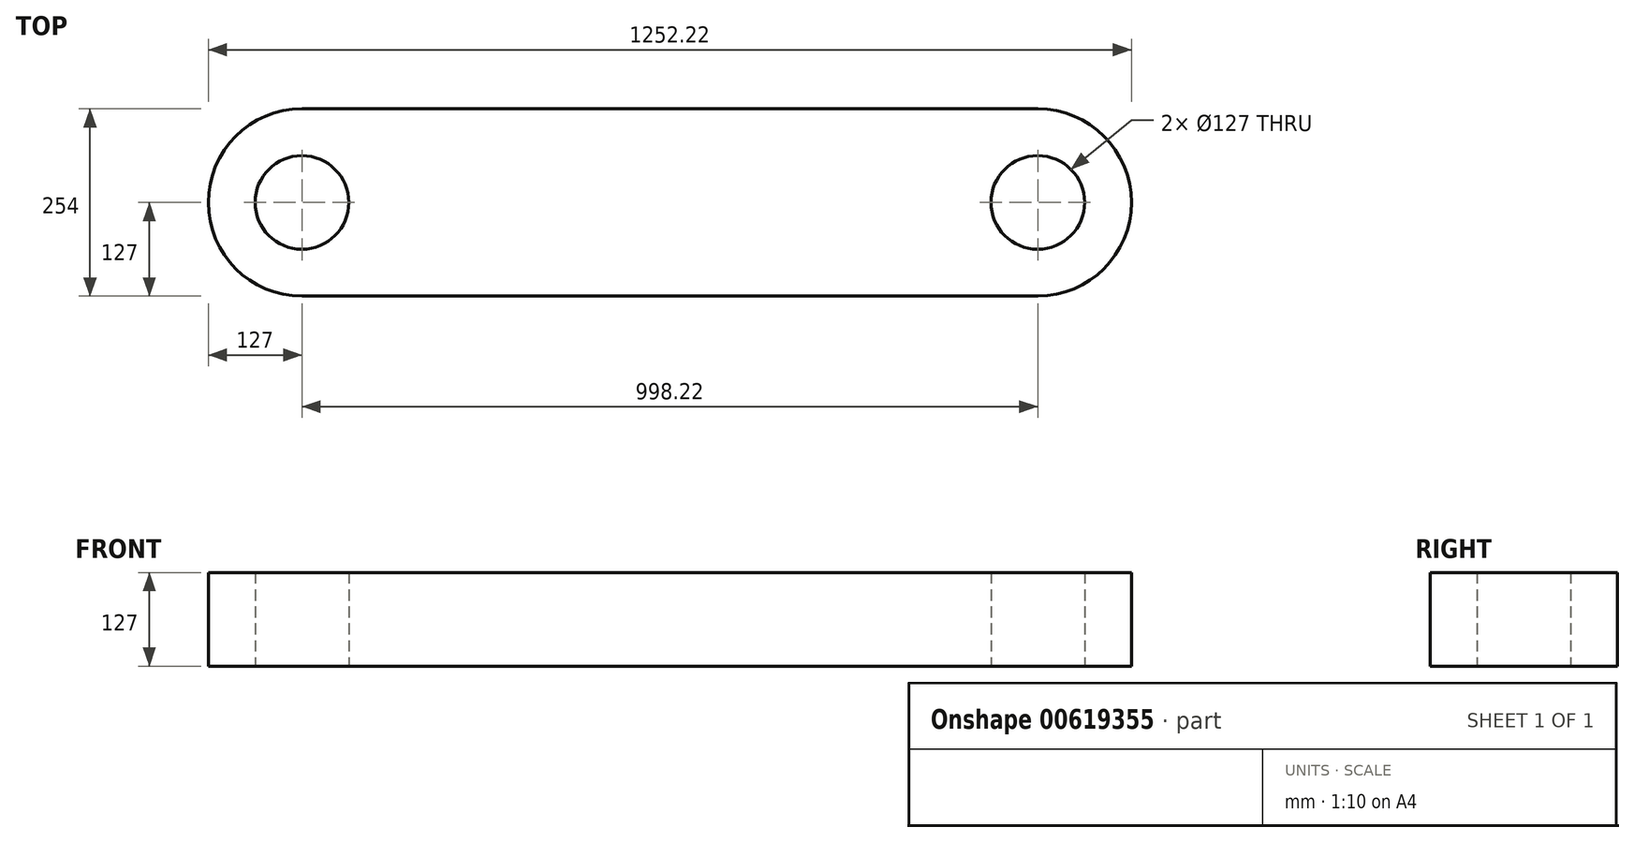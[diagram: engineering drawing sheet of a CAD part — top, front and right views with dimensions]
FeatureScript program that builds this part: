
annotation { "Feature Type Name" : "Feature", "Feature Type Description" : "" }
export const myFeature = defineFeature(function(context is Context, id is Id, definition is map)
    precondition{}
    {
        {
            var Q0;
            Q0=qCreatedBy(makeId("Top.planeOp"),FACE);
            var sketch = newSketch(context, id + "F0", { "sketchPlane" : qUnion([Q0])});
            skCircle(sketch, "E0", {"center": v(-486.41, 0) * mm, "radius": 63.5 * mm});
            skCircle(sketch, "E1", {"center": v(511.81, 0) * mm, "radius": 63.5 * mm});
            skLineSegment(sketch, "E2.bottom", {"start": v(-486.4, 127) * mm, "end": v(511.81, 127) * mm});
            skLineSegment(sketch, "E2.top", {"start": v(-486.4, -127) * mm, "end": v(511.81, -127) * mm});
            skArc(sketch, "E3", {"start": v(-486.4, 127) * mm, "mid": v(-613.4, 0) * mm, "end": v(-486.41, -127) * mm});
            skArc(sketch, "E4", {"start": v(511.81, -127) * mm, "mid": v(638.81, 0) * mm, "end": v(511.81, 127) * mm});
            skSolve(sketch);
        }
        {
            var Q0;
            Q0 = qSketchRegion(id + "F0", true);
            extrude(context, id + "F1", {"entities" : qUnion([Q0]), "depth" : 127 * mm, "offsetDistance" : 25.4 * mm});
        }
    });
